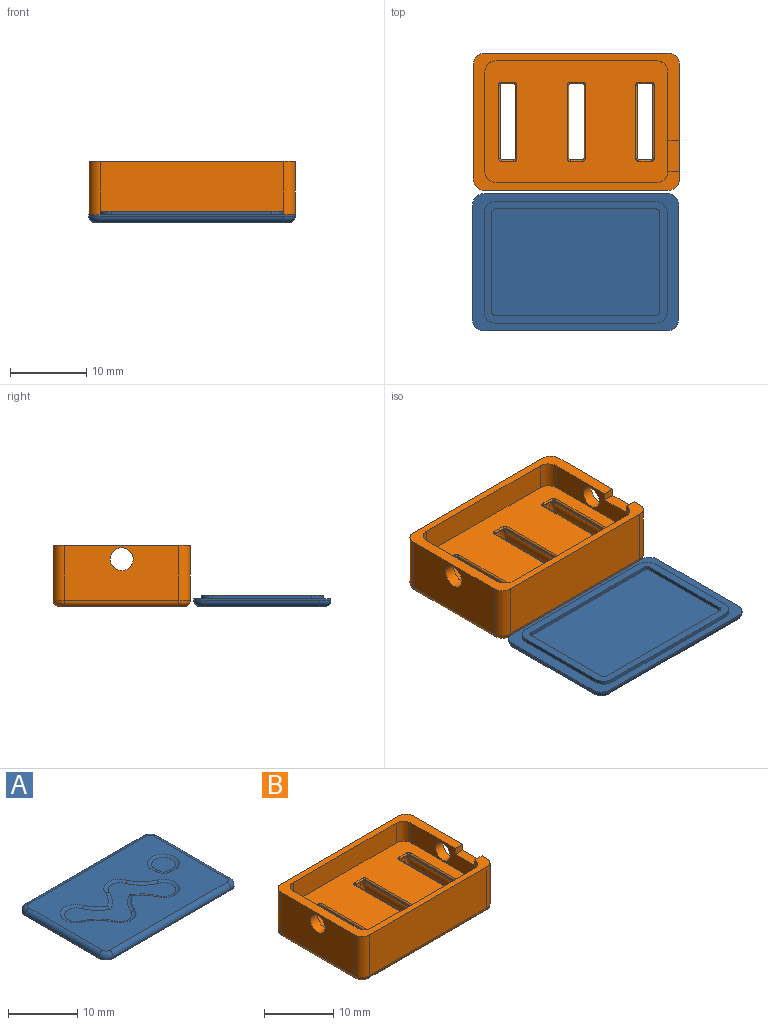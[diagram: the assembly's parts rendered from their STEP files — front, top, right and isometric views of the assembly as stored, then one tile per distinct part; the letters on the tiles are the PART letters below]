
ASSEMBLY  parts=2 mates=1
PART A: 52 faces, bbox 27.1x18.1x1.7 mm
  f0: plane 25.48x16.48mm, normal (0,0,1), area 308.8mm2, adj f10,f11,f12,f13,f14,f15,f16,f17
  f1: plane 27x18mm, normal (0,0,-1), area 102mm2, adj f2,f3,f4,f5,f6,f7,f8,f9
  f2: plane 15x0.2mm, normal (1,0,0), area 3mm2, adj f1,f3,f9,f17
  f3: cylinder r=1.5mm len=1.5mm, axis (0,0,-1), area 0.5mm2, adj f1,f2,f4,f16
  f4: plane 24x0.2mm, normal (0,1,0), area 4.8mm2, adj f1,f3,f5,f14
  f5: cylinder r=1.5mm len=1.5mm, axis (0,0,-1), area 0.5mm2, adj f1,f4,f6,f12
  f6: plane 15x0.2mm, normal (-1,0,0), area 3mm2, adj f1,f5,f7,f10
  f7: cylinder r=1.5mm len=1.5mm, axis (0,0,-1), area 0.5mm2, adj f1,f6,f8,f11
  f8: plane 24x0.2mm, normal (0,-1,0), area 4.8mm2, adj f1,f7,f9,f13
  f9: cylinder r=1.5mm len=1.5mm, axis (0,0,-1), area 0.5mm2, adj f1,f2,f8,f15
  f10: cylinder r=0.8mm len=15mm, axis (0,1,0), area 18.8mm2, adj f0,f6,f11,f12
  f11: torus R=0.7mm, axis (0,0,1), area 2.4mm2, adj f0,f7,f10,f13
  f12: torus R=0.7mm, axis (0,0,1), area 2.4mm2, adj f0,f5,f10,f14
  f13: cylinder r=0.8mm len=24mm, axis (-1,0,0), area 30.2mm2, adj f0,f8,f11,f15
  f14: cylinder r=0.8mm len=24mm, axis (1,0,0), area 30.2mm2, adj f0,f4,f12,f16
  f15: torus R=0.7mm, axis (0,0,1), area 2.4mm2, adj f0,f9,f13,f17
  f16: torus R=0.7mm, axis (0,0,1), area 2.4mm2, adj f0,f3,f14,f17
  f17: cylinder r=0.8mm len=15mm, axis (0,-1,0), area 18.8mm2, adj f0,f2,f15,f16
  f18: plane 13x0.5mm, normal (1,0,0), area 6.5mm2, adj f1,f19,f33,f34
  f19: cylinder r=1.5mm len=1.5mm, axis (0,0,1), area 1.2mm2, adj f1,f18,f20,f34
  f20: plane 21x0.5mm, normal (0,1,0), area 10.5mm2, adj f1,f19,f21,f34
  f21: cylinder r=1.5mm len=1.5mm, axis (0,0,1), area 1.2mm2, adj f1,f20,f22,f34
  f22: plane 13x0.5mm, normal (-1,0,0), area 6.5mm2, adj f1,f21,f23,f34
  f23: cylinder r=1.5mm len=1.5mm, axis (0,0,1), area 1.2mm2, adj f1,f22,f24,f34
  f24: plane 21x0.5mm, normal (0,-1,0), area 10.5mm2, adj f1,f23,f33,f34
  f25: plane 21x0.5mm, normal (0,-1,0), area 10.5mm2, adj f26,f32,f34,f35
  f26: cylinder r=0.5mm len=0.5mm, axis (0,0,1), area 0.4mm2, adj f25,f27,f34,f35
  f27: plane 13x0.5mm, normal (-1,0,0), area 6.5mm2, adj f26,f28,f34,f35
  f28: cylinder r=0.5mm len=0.5mm, axis (0,0,1), area 0.4mm2, adj f27,f29,f34,f35
  f29: plane 21x0.5mm, normal (0,1,0), area 10.5mm2, adj f28,f30,f34,f35
  f30: cylinder r=0.5mm len=0.5mm, axis (0,0,1), area 0.4mm2, adj f29,f31,f34,f35
  f31: plane 13x0.5mm, normal (1,0,0), area 6.5mm2, adj f30,f32,f34,f35
  f32: cylinder r=0.5mm len=0.5mm, axis (0,0,1), area 0.4mm2, adj f25,f31,f34,f35
  f33: cylinder r=1.5mm len=1.5mm, axis (0,0,1), area 1.2mm2, adj f1,f18,f24,f34
  f34: plane 24x16mm, normal (0,0,-1), area 74.3mm2, adj f18,f19,f20,f21,f22,f23,f24,f25
  f35: plane 22x14mm, normal (0,0,-1), area 307.8mm2, adj f25,f26,f27,f28,f29,f30,f31,f32
  f36: plane 3.43x3.43mm, normal (0,0,1), area 9.4mm2, adj f49,f50,f51
  f37: plane 16.77x7.88mm, normal (0,0,1), area 59.5mm2, adj f38,f39,f40,f41,f42,f43,f44,f45
  f38: torus R=1.72mm, axis (0,0,-1), area 3.3mm2, adj f0,f37,f39,f40
  f39: bspline ~4.28x4.15mm, area 2.5mm2, adj f0,f37,f38,f41
  f40: bspline ~3.89x3.81mm, area 3mm2, adj f0,f37,f38,f42
  f41: bspline ~4.27x4.22mm, area 2.5mm2, adj f0,f37,f39,f43
  f42: torus R=1.72mm, axis (0,0,-1), area 5.1mm2, adj f0,f37,f40,f44
  f43: torus R=1.72mm, axis (0,0,-1), area 5.3mm2, adj f0,f37,f41,f45
  f44: bspline ~4.31x4.16mm, area 2.6mm2, adj f0,f37,f42,f46
  f45: bspline ~3.68x3.62mm, area 3mm2, adj f0,f37,f43,f47
  f46: bspline ~4.31x4.16mm, area 2.6mm2, adj f0,f37,f44,f47
  f47: torus R=1.72mm, axis (0,0,-1), area 3.1mm2, adj f0,f37,f45,f46
  f48: bspline ~0.55x0.55mm, area 0.1mm2, adj f0,f49,f50
  f49: cylinder r=1mm len=1.25mm, axis (0.97,-0.25,0), area 0.7mm2, adj f0,f36,f48,f51
  f50: cylinder r=1mm len=1.25mm, axis (0.25,-0.97,0), area 0.7mm2, adj f0,f36,f48,f51
  f51: torus R=1.72mm, axis (0,0,-1), area 6.8mm2, adj f0,f36,f49,f50
PART B: 149 faces, bbox 27x18x8 mm
  f0: plane 0.8x0.12mm, normal (0,1,0), area 0mm2, adj f127,f136,f137
  f1: plane 0.8x0.12mm, normal (0,-1,0), area 0mm2, adj f105,f114,f115
  f2: plane 0.8x0.12mm, normal (0,1,0), area 0mm2, adj f107,f116,f117
  f3: plane 0.8x0.12mm, normal (0,-1,0), area 0mm2, adj f85,f94,f95
  f4: plane 0.8x0.12mm, normal (0,1,0), area 0mm2, adj f87,f96,f97
  f5: plane 0.8x0.12mm, normal (0,-1,0), area 0mm2, adj f125,f134,f135
  f6: cylinder r=2.6mm len=12.7mm, axis (0,1,0), area 101.6mm2, adj f35,f39,f40,f44,f101,f102,f103,f105
  f7: cylinder r=2.6mm len=12.7mm, axis (0,1,0), area 101.6mm2, adj f45,f49,f50,f54,f121,f122,f123,f125
  f8: cylinder r=2.6mm len=12.7mm, axis (0,1,0), area 101.6mm2, adj f55,f59,f60,f64,f81,f82,f83,f85
  f9: plane 24x16mm, normal (0,0,1), area 307.6mm2, adj f12,f65,f66,f67,f68,f69,f70,f71
  f10: plane 27x18mm, normal (0,0,1), area 96mm2, adj f11,f12,f26,f27,f28,f65,f66,f67
  f11: plane 15x7.2mm, normal (1,0,0), area 96.9mm2, adj f10,f73,f74,f75,f76,f78,f80,f148
  f12: plane 13x3.5mm, normal (-1,0,0), area 34.4mm2, adj f9,f10,f65,f71,f73,f75,f76
  f13: plane 9.6x0.27mm, normal (1,0,0), area 2.6mm2, adj f106,f115,f116,f120
  f14: plane 9.6x0.27mm, normal (-1,0,0), area 2.6mm2, adj f101,f104,f108,f109
  f15: plane 0.8x0.12mm, normal (0,-1,0), area 0mm2, adj f104,f105,f114
  f16: plane 0.8x0.12mm, normal (0,1,0), area 0mm2, adj f107,f108,f117
  f17: plane 9.6x0.27mm, normal (1,0,0), area 2.6mm2, adj f126,f135,f136,f140
  f18: plane 9.6x0.27mm, normal (-1,0,0), area 2.6mm2, adj f121,f124,f128,f129
  f19: plane 0.8x0.12mm, normal (0,-1,0), area 0mm2, adj f124,f125,f134
  f20: plane 0.8x0.12mm, normal (0,1,0), area 0mm2, adj f127,f128,f137
  f21: plane 9.6x0.27mm, normal (1,0,0), area 2.6mm2, adj f86,f95,f96,f100
  f22: plane 9.6x0.27mm, normal (-1,0,0), area 2.6mm2, adj f81,f84,f88,f89
  f23: plane 0.8x0.12mm, normal (0,-1,0), area 0mm2, adj f84,f85,f94
  f24: plane 0.8x0.12mm, normal (0,1,0), area 0mm2, adj f87,f88,f97
  f25: plane 25.4x16.4mm, normal (0,0,-1), area 160.1mm2, adj f35,f36,f37,f38,f41,f42,f43,f44
  f26: plane 15x7.2mm, normal (-1,0,0), area 100.9mm2, adj f10,f72,f77,f79,f141
  f27: plane 24x7.2mm, normal (0,-1,0), area 172.8mm2, adj f10,f79,f80,f144
  f28: plane 24x7.2mm, normal (0,1,0), area 172.8mm2, adj f10,f77,f78,f145
  f29: plane 4.2x3.1mm, normal (0,1,0), area 11mm2, adj f58,f59
  f30: plane 4.2x3.1mm, normal (0,-1,0), area 11mm2, adj f60,f61
  f31: plane 4.2x3.1mm, normal (0,1,0), area 11mm2, adj f48,f49
  f32: plane 4.2x3.1mm, normal (0,-1,0), area 11mm2, adj f50,f51
  f33: plane 4.2x3.1mm, normal (0,1,0), area 11mm2, adj f38,f39
  f34: plane 4.2x3.1mm, normal (0,-1,0), area 11mm2, adj f40,f41
  f35: cylinder r=0.5mm len=12.7mm, axis (0,1,0), area 12.1mm2, adj f6,f25,f36,f37
  f36: bspline ~1.17x1.07mm, area 1mm2, adj f25,f35,f38,f39
  f37: bspline ~1.21x1.2mm, area 1mm2, adj f25,f35,f40,f41
  f38: cylinder r=0.5mm len=3.69mm, axis (1,0,0), area 2.9mm2, adj f25,f33,f36,f42
  f39: torus R=2.1mm, axis (0,-1,0), area 7.4mm2, adj f6,f33,f36,f42
  f40: torus R=2.1mm, axis (0,-1,0), area 7.4mm2, adj f6,f34,f37,f43
  f41: cylinder r=0.5mm len=3.69mm, axis (-1,0,0), area 2.9mm2, adj f25,f34,f37,f43
  f42: bspline ~1.21x1.2mm, area 1mm2, adj f25,f38,f39,f44
  f43: bspline ~1.17x1.07mm, area 1mm2, adj f25,f40,f41,f44
  f44: cylinder r=0.5mm len=12.7mm, axis (0,1,0), area 12.1mm2, adj f6,f25,f42,f43
  f45: cylinder r=0.5mm len=12.7mm, axis (0,1,0), area 12.1mm2, adj f7,f25,f46,f47
  f46: bspline ~1.17x1.07mm, area 1mm2, adj f25,f45,f48,f49
  f47: bspline ~1.21x1.2mm, area 1mm2, adj f25,f45,f50,f51
  f48: cylinder r=0.5mm len=3.69mm, axis (1,0,0), area 2.9mm2, adj f25,f31,f46,f52
  f49: torus R=2.1mm, axis (0,-1,0), area 7.4mm2, adj f7,f31,f46,f52
  f50: torus R=2.1mm, axis (0,-1,0), area 7.4mm2, adj f7,f32,f47,f53
  f51: cylinder r=0.5mm len=3.69mm, axis (-1,0,0), area 2.9mm2, adj f25,f32,f47,f53
  f52: bspline ~1.21x1.2mm, area 1mm2, adj f25,f48,f49,f54
  f53: bspline ~1.17x1.07mm, area 1mm2, adj f25,f50,f51,f54
  f54: cylinder r=0.5mm len=12.7mm, axis (0,1,0), area 12.1mm2, adj f7,f25,f52,f53
  f55: cylinder r=0.5mm len=12.7mm, axis (0,1,0), area 12.1mm2, adj f8,f25,f56,f57
  f56: bspline ~1.17x1.07mm, area 1mm2, adj f25,f55,f58,f59
  f57: bspline ~1.21x1.2mm, area 1mm2, adj f25,f55,f60,f61
  f58: cylinder r=0.5mm len=3.69mm, axis (1,0,0), area 2.9mm2, adj f25,f29,f56,f62
  f59: torus R=2.1mm, axis (0,-1,0), area 7.4mm2, adj f8,f29,f56,f62
  f60: torus R=2.1mm, axis (0,-1,0), area 7.4mm2, adj f8,f30,f57,f63
  f61: cylinder r=0.5mm len=3.69mm, axis (-1,0,0), area 2.9mm2, adj f25,f30,f57,f63
  f62: bspline ~1.21x1.2mm, area 1mm2, adj f25,f58,f59,f64
  f63: bspline ~1.17x1.07mm, area 1mm2, adj f25,f60,f61,f64
  f64: cylinder r=0.5mm len=12.7mm, axis (0,1,0), area 12.1mm2, adj f8,f25,f62,f63
  f65: cylinder r=1.5mm len=3.5mm, axis (0,0,1), area 8.2mm2, adj f9,f10,f12,f66
  f66: plane 21x3.5mm, normal (0,-1,0), area 73.5mm2, adj f9,f10,f65,f67
  f67: cylinder r=1.5mm len=3.5mm, axis (0,0,1), area 8.2mm2, adj f9,f10,f66,f68
  f68: plane 13x3.5mm, normal (1,0,0), area 38.4mm2, adj f9,f10,f67,f69,f72
  f69: cylinder r=1.5mm len=3.5mm, axis (0,0,1), area 8.2mm2, adj f9,f10,f68,f70
  f70: plane 21x3.5mm, normal (0,1,0), area 73.5mm2, adj f9,f10,f69,f71
  f71: cylinder r=1.5mm len=3.5mm, axis (0,0,1), area 8.2mm2, adj f9,f10,f12,f70,f74
  f72: cylinder r=1.5mm len=3mm, axis (1,0,0), area 14.1mm2, adj f26,f68
  f73: cylinder r=1.5mm len=3mm, axis (1,0,0), area 14.1mm2, adj f11,f12
  f74: plane 1.5x1mm, normal (0,1,0), area 1.5mm2, adj f10,f11,f71,f75
  f75: plane 4x1.5mm, normal (0,0,1), area 6mm2, adj f11,f12,f74,f76
  f76: plane 1.5x1mm, normal (0,-1,0), area 1.5mm2, adj f10,f11,f12,f75
  f77: cylinder r=1.5mm len=7.2mm, axis (0,0,-1), area 17mm2, adj f10,f26,f28,f143
  f78: cylinder r=1.5mm len=7.2mm, axis (0,0,1), area 17mm2, adj f10,f11,f28,f147
  f79: cylinder r=1.5mm len=7.2mm, axis (0,0,1), area 17mm2, adj f10,f26,f27,f142
  f80: cylinder r=1.5mm len=7.2mm, axis (0,0,-1), area 17mm2, adj f10,f11,f27,f146
  f81: cylinder r=0.2mm len=9.6mm, axis (0,1,0), area 2.2mm2, adj f8,f22,f82,f83
  f82: bspline ~0.48x0.42mm, area 0.1mm2, adj f8,f81,f84,f85
  f83: bspline ~0.46x0.42mm, area 0.1mm2, adj f8,f81,f87,f88
  f84: cylinder r=0.2mm len=0.27mm, axis (0,0,1), area 0.1mm2, adj f22,f23,f82,f90
  f85: torus R=2.8mm, axis (0,-1,0), area 0.5mm2, adj f3,f8,f23,f82,f91
  f86: cylinder r=0.2mm len=9.6mm, axis (0,1,0), area 2.2mm2, adj f8,f21,f91,f92
  f87: torus R=2.8mm, axis (0,-1,0), area 0.5mm2, adj f4,f8,f24,f83,f92
  f88: cylinder r=0.2mm len=0.27mm, axis (0,0,-1), area 0.1mm2, adj f22,f24,f83,f93
  f89: cylinder r=0.2mm len=9.6mm, axis (0,-1,0), area 3mm2, adj f9,f22,f90,f93
  f90: torus R=0.4mm, axis (0,0,1), area 0.1mm2, adj f9,f84,f89,f94
  f91: bspline ~0.46x0.42mm, area 0.1mm2, adj f8,f85,f86,f95
  f92: bspline ~0.48x0.42mm, area 0.1mm2, adj f8,f86,f87,f96
  f93: torus R=0.4mm, axis (0,0,1), area 0.1mm2, adj f9,f88,f89,f97
  f94: cylinder r=0.2mm len=1.6mm, axis (1,0,0), area 0.5mm2, adj f3,f9,f23,f90,f98
  f95: cylinder r=0.2mm len=0.27mm, axis (0,0,-1), area 0.1mm2, adj f3,f21,f91,f98
  f96: cylinder r=0.2mm len=0.27mm, axis (0,0,1), area 0.1mm2, adj f4,f21,f92,f99
  f97: cylinder r=0.2mm len=1.6mm, axis (-1,0,0), area 0.5mm2, adj f4,f9,f24,f93,f99
  f98: torus R=0.4mm, axis (0,0,1), area 0.1mm2, adj f9,f94,f95,f100
  f99: torus R=0.4mm, axis (0,0,1), area 0.1mm2, adj f9,f96,f97,f100
  f100: cylinder r=0.2mm len=9.6mm, axis (0,1,0), area 3mm2, adj f9,f21,f98,f99
  f101: cylinder r=0.2mm len=9.6mm, axis (0,1,0), area 2.2mm2, adj f6,f14,f102,f103
  f102: bspline ~0.48x0.42mm, area 0.1mm2, adj f6,f101,f104,f105
  f103: bspline ~0.46x0.42mm, area 0.1mm2, adj f6,f101,f107,f108
  f104: cylinder r=0.2mm len=0.27mm, axis (0,0,1), area 0.1mm2, adj f14,f15,f102,f110
  f105: torus R=2.8mm, axis (0,-1,0), area 0.5mm2, adj f1,f6,f15,f102,f111
  f106: cylinder r=0.2mm len=9.6mm, axis (0,1,0), area 2.2mm2, adj f6,f13,f111,f112
  f107: torus R=2.8mm, axis (0,-1,0), area 0.5mm2, adj f2,f6,f16,f103,f112
  f108: cylinder r=0.2mm len=0.27mm, axis (0,0,-1), area 0.1mm2, adj f14,f16,f103,f113
  f109: cylinder r=0.2mm len=9.6mm, axis (0,-1,0), area 3mm2, adj f9,f14,f110,f113
  f110: torus R=0.4mm, axis (0,0,1), area 0.1mm2, adj f9,f104,f109,f114
  f111: bspline ~0.46x0.42mm, area 0.1mm2, adj f6,f105,f106,f115
  f112: bspline ~0.48x0.42mm, area 0.1mm2, adj f6,f106,f107,f116
  f113: torus R=0.4mm, axis (0,0,1), area 0.1mm2, adj f9,f108,f109,f117
  f114: cylinder r=0.2mm len=1.6mm, axis (1,0,0), area 0.5mm2, adj f1,f9,f15,f110,f118
  f115: cylinder r=0.2mm len=0.27mm, axis (0,0,-1), area 0.1mm2, adj f1,f13,f111,f118
  f116: cylinder r=0.2mm len=0.27mm, axis (0,0,1), area 0.1mm2, adj f2,f13,f112,f119
  f117: cylinder r=0.2mm len=1.6mm, axis (-1,0,0), area 0.5mm2, adj f2,f9,f16,f113,f119
  f118: torus R=0.4mm, axis (0,0,1), area 0.1mm2, adj f9,f114,f115,f120
  f119: torus R=0.4mm, axis (0,0,1), area 0.1mm2, adj f9,f116,f117,f120
  f120: cylinder r=0.2mm len=9.6mm, axis (0,1,0), area 3mm2, adj f9,f13,f118,f119
  f121: cylinder r=0.2mm len=9.6mm, axis (0,1,0), area 2.2mm2, adj f7,f18,f122,f123
  f122: bspline ~0.48x0.42mm, area 0.1mm2, adj f7,f121,f124,f125
  f123: bspline ~0.46x0.42mm, area 0.1mm2, adj f7,f121,f127,f128
  f124: cylinder r=0.2mm len=0.27mm, axis (0,0,1), area 0.1mm2, adj f18,f19,f122,f130
  f125: torus R=2.8mm, axis (0,-1,0), area 0.5mm2, adj f5,f7,f19,f122,f131
  f126: cylinder r=0.2mm len=9.6mm, axis (0,1,0), area 2.2mm2, adj f7,f17,f131,f132
  f127: torus R=2.8mm, axis (0,-1,0), area 0.5mm2, adj f0,f7,f20,f123,f132
  f128: cylinder r=0.2mm len=0.27mm, axis (0,0,-1), area 0.1mm2, adj f18,f20,f123,f133
  f129: cylinder r=0.2mm len=9.6mm, axis (0,-1,0), area 3mm2, adj f9,f18,f130,f133
  f130: torus R=0.4mm, axis (0,0,1), area 0.1mm2, adj f9,f124,f129,f134
  f131: bspline ~0.46x0.42mm, area 0.1mm2, adj f7,f125,f126,f135
  f132: bspline ~0.48x0.42mm, area 0.1mm2, adj f7,f126,f127,f136
  f133: torus R=0.4mm, axis (0,0,1), area 0.1mm2, adj f9,f128,f129,f137
  f134: cylinder r=0.2mm len=1.6mm, axis (1,0,0), area 0.5mm2, adj f5,f9,f19,f130,f138
  f135: cylinder r=0.2mm len=0.27mm, axis (0,0,-1), area 0.1mm2, adj f5,f17,f131,f138
  f136: cylinder r=0.2mm len=0.27mm, axis (0,0,1), area 0.1mm2, adj f0,f17,f132,f139
  f137: cylinder r=0.2mm len=1.6mm, axis (-1,0,0), area 0.5mm2, adj f0,f9,f20,f133,f139
  f138: torus R=0.4mm, axis (0,0,1), area 0.1mm2, adj f9,f134,f135,f140
  f139: torus R=0.4mm, axis (0,0,1), area 0.1mm2, adj f9,f136,f137,f140
  f140: cylinder r=0.2mm len=9.6mm, axis (0,1,0), area 3mm2, adj f9,f17,f138,f139
  f141: cylinder r=0.8mm len=15mm, axis (0,1,0), area 18.8mm2, adj f25,f26,f142,f143
  f142: torus R=0.7mm, axis (0,0,1), area 2.4mm2, adj f25,f79,f141,f144
  f143: torus R=0.7mm, axis (0,0,1), area 2.4mm2, adj f25,f77,f141,f145
  f144: cylinder r=0.8mm len=24mm, axis (-1,0,0), area 30.2mm2, adj f25,f27,f142,f146
  f145: cylinder r=0.8mm len=24mm, axis (1,0,0), area 30.2mm2, adj f25,f28,f143,f147
  f146: torus R=0.7mm, axis (0,0,1), area 2.4mm2, adj f25,f80,f144,f148
  f147: torus R=0.7mm, axis (0,0,1), area 2.4mm2, adj f25,f78,f145,f148
  f148: cylinder r=0.8mm len=15mm, axis (0,-1,0), area 18.8mm2, adj f11,f25,f146,f147
PLACE A rot(axis=(1,0,0),180deg) t=(-0.1,-18.42,6)mm
PLACE B at identity fixed
MATE planar B.f25 <-> A.f0  axis (0,0,-1) through (0,0,-1.5)mm
